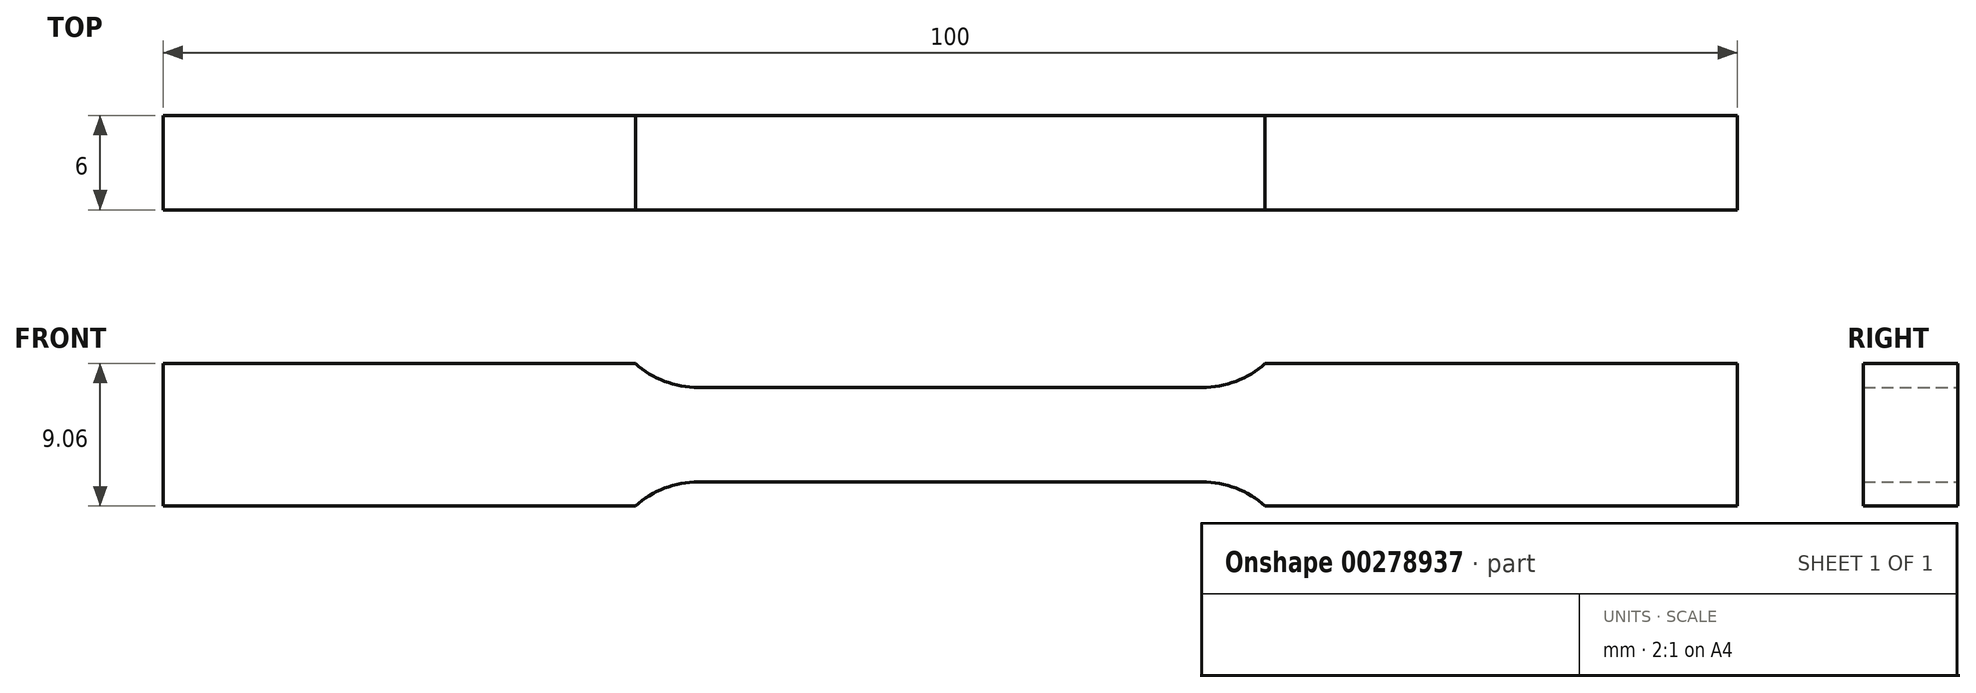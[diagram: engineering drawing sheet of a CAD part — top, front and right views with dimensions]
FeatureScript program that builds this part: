
annotation { "Feature Type Name" : "Feature", "Feature Type Description" : "" }
export const myFeature = defineFeature(function(context is Context, id is Id, definition is map)
    precondition{}
    {
        {
            var Q0;
            Q0=qCreatedBy(makeId("Front.planeOp"),FACE);
            var sketch = newSketch(context, id + "F0", { "sketchPlane" : qUnion([Q0])});
            skLineSegment(sketch, "E0", {"start": v(0, 3) * mm, "end": v(16, 3) * mm});
            skArc(sketch, "E1", {"start": v(16, 3) * mm, "mid": v(18.14, 3.4) * mm, "end": v(20, 4.53) * mm});
            skLineSegment(sketch, "E2", {"start": v(20, 4.53) * mm, "end": v(50, 4.53) * mm});
            skLineSegment(sketch, "E3", {"start": v(50, 4.53) * mm, "end": v(50, 0) * mm});
            skLineSegment(sketch, "E4.MirrorCS", {"start": v(0, -3) * mm, "end": v(16, -3) * mm});
            skLineSegment(sketch, "E5.MirrorCS", {"start": v(50, -4.53) * mm, "end": v(50, 0) * mm});
            skLineSegment(sketch, "E6.MirrorCS", {"start": v(20, -4.53) * mm, "end": v(50, -4.53) * mm});
            skArc(sketch, "E7.MirrorCS", {"start": v(16, -3) * mm, "mid": v(18.14, -3.4) * mm, "end": v(20, -4.53) * mm});
            skArc(sketch, "E8.MirrorCS", {"start": v(-16, -3) * mm, "mid": v(-18.14, -3.4) * mm, "end": v(-20, -4.53) * mm});
            skLineSegment(sketch, "E9.MirrorCS", {"start": v(-20, -4.53) * mm, "end": v(-50, -4.53) * mm});
            skArc(sketch, "E10.MirrorCS", {"start": v(-16, 3) * mm, "mid": v(-18.14, 3.4) * mm, "end": v(-20, 4.53) * mm});
            skLineSegment(sketch, "E11.MirrorCS", {"start": v(-20, 4.53) * mm, "end": v(-50, 4.53) * mm});
            skLineSegment(sketch, "E12.MirrorCS", {"start": v(-50, -4.53) * mm, "end": v(-50, 0) * mm});
            skLineSegment(sketch, "E13.MirrorCS", {"start": v(0, -3) * mm, "end": v(-16, -3) * mm});
            skLineSegment(sketch, "E14.MirrorCS", {"start": v(-50, 4.53) * mm, "end": v(-50, 0) * mm});
            skLineSegment(sketch, "E15.MirrorCS", {"start": v(0, 3) * mm, "end": v(-16, 3) * mm});
            skSolve(sketch);
        }
        {
            var Q0;
            Q0 = qSketchRegion(id + "F0", true);
            extrude(context, id + "F1", {"entities" : qUnion([Q0]), "endBound" : BoundingType.SYMMETRIC, "depth" : 6 * mm});
        }
    });
